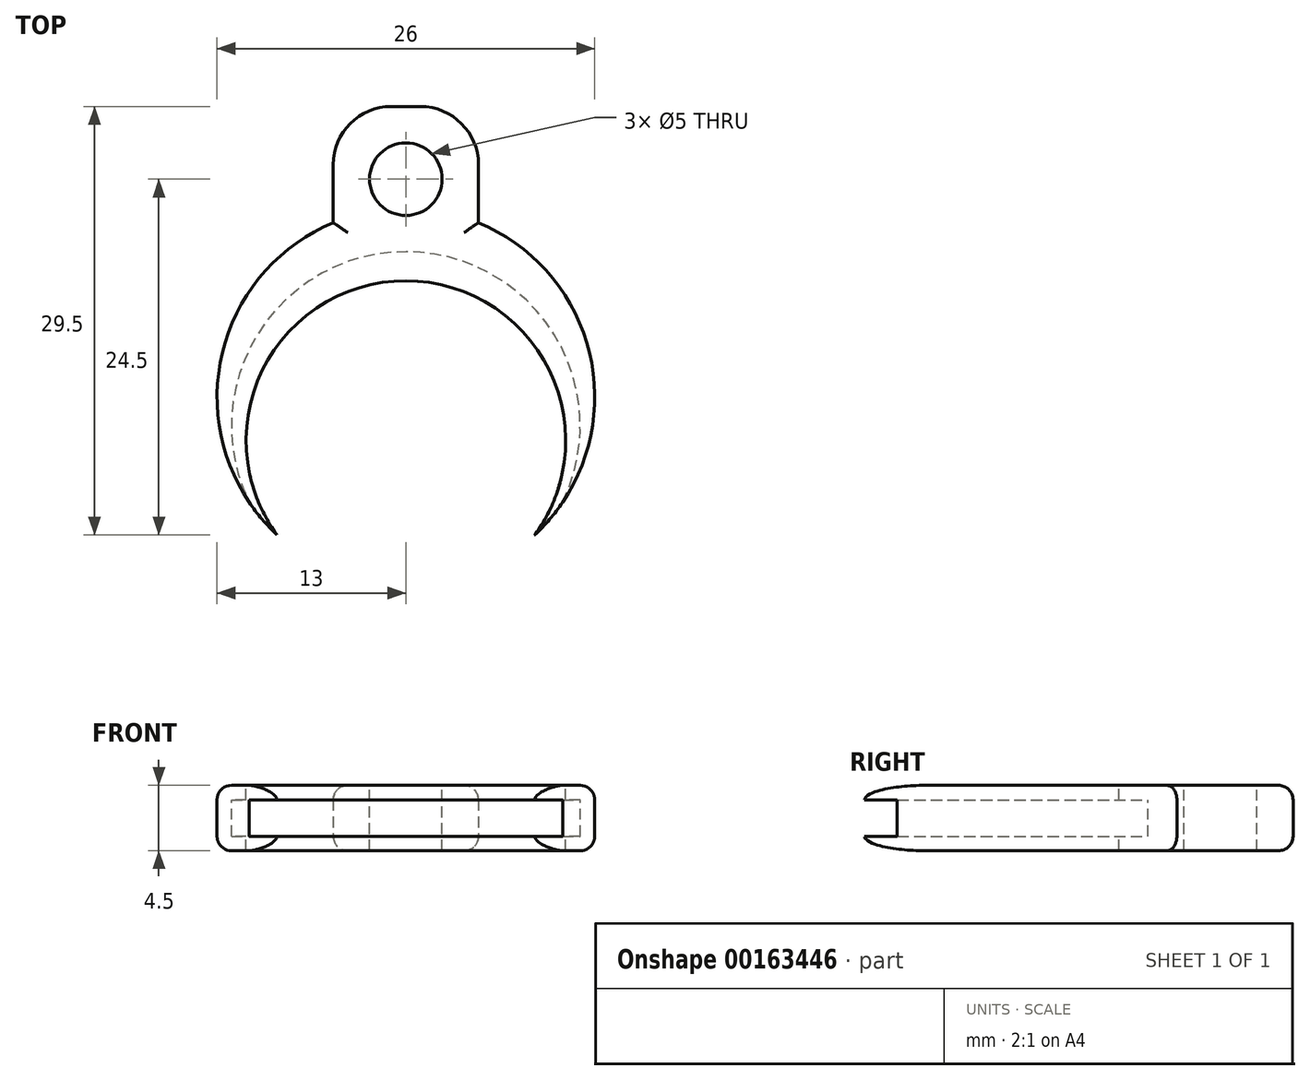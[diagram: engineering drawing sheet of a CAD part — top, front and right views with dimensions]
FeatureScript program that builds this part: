
annotation { "Feature Type Name" : "Feature", "Feature Type Description" : "" }
export const myFeature = defineFeature(function(context is Context, id is Id, definition is map)
    precondition{}
    {
        {
            var Q0;
            Q0=qCreatedBy(makeId("Top.planeOp"),FACE);
            var sketch = newSketch(context, id + "F0", { "sketchPlane" : qUnion([Q0])});
            skCircle(sketch, "E0", {"center": v(0, 0) * mm, "radius": 13 * mm});
            skLineSegment(sketch, "E1.bottom", {"start": v(-5, 12) * mm, "end": v(5, 12) * mm});
            skLineSegment(sketch, "E1.top", {"start": v(-5, 20) * mm, "end": v(5, 20) * mm});
            skLineSegment(sketch, "E1.left", {"start": v(-5, 12) * mm, "end": v(-5, 20) * mm});
            skLineSegment(sketch, "E1.right", {"start": v(5, 12) * mm, "end": v(5, 20) * mm});
            skSolve(sketch);
        }
        {
            var Q0;
            Q0 = qSketchRegion(id + "F0", true);
            extrude(context, id + "F1", {"entities" : qUnion([Q0]), "depth" : 4.5 * mm});
        }
        {
            var Q0;
            Q0=makeQuery(id+"F1.opExtrude","SWEPT_EDGE",EDGE,{"disambiguationData":[OSD([sQuery(id+"F0.wireOp",EDGE,"E1.top"),sQuery(id+"F0.wireOp",EDGE,"E1.right")])]});
            var Q1;
            Q1=makeQuery(id+"F1.opExtrude","SWEPT_EDGE",EDGE,{"disambiguationData":[OSD([sQuery(id+"F0.wireOp",EDGE,"E1.top"),sQuery(id+"F0.wireOp",EDGE,"E1.left")])]});
            fillet(context, id + "F2", {"entities" : qUnion([Q0, Q1]), "radius" : 4 * mm, "tangentPropagation" : true, "allowEdgeOverflow" : false});
        }
        {
            var Q0;
            Q0=makeQuery(id+"F1.opExtrude","CAP_FACE",FACE,{"disambiguationData":[OSD([sQuery(id+"F0.wireOp",EDGE,"E0"),sQuery(id+"F0.wireOp",EDGE,"E1.top"),sQuery(id+"F0.wireOp",EDGE,"E1.left"),sQuery(id+"F0.wireOp",EDGE,"E1.right")])],"isStart":false});
            var sketch = newSketch(context, id + "F3", { "sketchPlane" : qUnion([Q0])});
            skCircle(sketch, "E2", {"center": v(0, 15) * mm, "radius": 2.5 * mm});
            skSolve(sketch);
        }
        {
            var Q0;
            Q0 = qSketchRegion(id + "F3", true);
            extrude(context, id + "F4", {"entities" : qUnion([Q0]), "operationType" : NewBodyOperationType.REMOVE, "endBound" : BoundingType.THROUGH_ALL, "oppositeDirection" : true, "depth" : 25 * mm});
        }
        {
            var Q0;
            Q0=makeQuery(id+"F1.opExtrude","CAP_FACE",FACE,{"disambiguationData":[OSD([sQuery(id+"F0.wireOp",EDGE,"E0"),sQuery(id+"F0.wireOp",EDGE,"E1.top"),sQuery(id+"F0.wireOp",EDGE,"E1.left"),sQuery(id+"F0.wireOp",EDGE,"E1.right")])],"isStart":false});
            var sketch = newSketch(context, id + "F5", { "sketchPlane" : qUnion([Q0])});
            skCircle(sketch, "E3", {"center": v(0, -3) * mm, "radius": 11 * mm});
            skSolve(sketch);
        }
        {
            var Q0;
            Q0 = qSketchRegion(id + "F5", true);
            extrude(context, id + "F6", {"entities" : qUnion([Q0]), "operationType" : NewBodyOperationType.REMOVE, "oppositeDirection" : true, "depth" : 1 * mm});
        }
        {
            var Q0;
            Q0=makeQuery(id+"F6.boolean.opBoolean","COPY",FACE,{"derivedFrom":makeQuery(id+"F6.opExtrude","CAP_FACE",FACE,{"disambiguationData":[OSD([sQuery(id+"F5.wireOp",EDGE,"E3")])],"isStart":false})});
            var sketch = newSketch(context, id + "F7", { "sketchPlane" : qUnion([Q0])});
            skCircle(sketch, "E4", {"center": v(0, -2) * mm, "radius": 12 * mm});
            skSolve(sketch);
        }
        {
            var Q0;
            Q0 = qSketchRegion(id + "F7", true);
            extrude(context, id + "F8", {"entities" : qUnion([Q0]), "operationType" : NewBodyOperationType.REMOVE, "oppositeDirection" : true, "depth" : 2.5 * mm});
        }
        {
            var Q0;
            Q0=makeQuery(id+"F8.boolean.opBoolean","COPY",FACE,{"derivedFrom":makeQuery(id+"F8.opExtrude","CAP_FACE",FACE,{"disambiguationData":[OSD([sQuery(id+"F7.wireOp",EDGE,"E4")])],"isStart":false})});
            var sketch = newSketch(context, id + "F9", { "sketchPlane" : qUnion([Q0])});
            skCircle(sketch, "E5", {"center": v(0, -3) * mm, "radius": 11 * mm});
            skSolve(sketch);
        }
        {
            var Q0;
            Q0 = qSketchRegion(id + "F9", true);
            extrude(context, id + "F10", {"entities" : qUnion([Q0]), "operationType" : NewBodyOperationType.REMOVE, "endBound" : BoundingType.THROUGH_ALL, "oppositeDirection" : true, "depth" : 25 * mm});
        }
        {
            var Q0;
            {var subQ0=sQuery(id+"F0.wireOp",EDGE,"E0");var subQ1=sQuery(id+"F0.wireOp",EDGE,"E1.right");Q0=makeQuery(id+"F6.boolean.opBoolean","SPLIT",EDGE,{"disambiguationData":[TD([makeQuery(id+"F1.opExtrude","SWEPT_FACE",FACE,{"disambiguationData":[OSD([subQ1])]})])],"derivedFrom":makeQuery(id+"F1.opExtrude","CAP_EDGE",EDGE,{"disambiguationData":[OSD([subQ0])],"isStart":false})});}
            var Q1;
            Q1=makeQuery(id+"F1.opExtrude","CAP_EDGE",EDGE,{"disambiguationData":[OSD([sQuery(id+"F0.wireOp",EDGE,"E1.right")])],"isStart":false});
            var Q2;
            {var subQ0=sQuery(id+"F0.wireOp",EDGE,"E0");var subQ1=sQuery(id+"F0.wireOp",EDGE,"E1.left");Q2=makeQuery(id+"F6.boolean.opBoolean","SPLIT",EDGE,{"disambiguationData":[TD([makeQuery(id+"F1.opExtrude","SWEPT_FACE",FACE,{"disambiguationData":[OSD([subQ1])]})])],"derivedFrom":makeQuery(id+"F1.opExtrude","CAP_EDGE",EDGE,{"disambiguationData":[OSD([subQ0])],"isStart":false})});}
            var Q3;
            {var subQ0=sQuery(id+"F0.wireOp",EDGE,"E0");var subQ1=sQuery(id+"F0.wireOp",EDGE,"E1.right");Q3=makeQuery(id+"F10.boolean.opBoolean","SPLIT",EDGE,{"disambiguationData":[TD([makeQuery(id+"F1.opExtrude","SWEPT_FACE",FACE,{"disambiguationData":[OSD([subQ1])]})])],"derivedFrom":makeQuery(id+"F1.opExtrude","CAP_EDGE",EDGE,{"disambiguationData":[OSD([subQ0])],"isStart":true})});}
            var Q4;
            {var subQ0=sQuery(id+"F0.wireOp",EDGE,"E0");var subQ1=sQuery(id+"F0.wireOp",EDGE,"E1.left");Q4=makeQuery(id+"F10.boolean.opBoolean","SPLIT",EDGE,{"disambiguationData":[TD([makeQuery(id+"F1.opExtrude","SWEPT_FACE",FACE,{"disambiguationData":[OSD([subQ1])]})])],"derivedFrom":makeQuery(id+"F1.opExtrude","CAP_EDGE",EDGE,{"disambiguationData":[OSD([subQ0])],"isStart":true})});}
            var Q5;
            {var subQ0=sQuery(id+"F0.wireOp",EDGE,"E1.left");var subQ1=sQuery(id+"F0.wireOp",EDGE,"E1.top");Q5=makeQuery(id+"F2.opFillet","BLEND_EDGE",EDGE,{"blendedFrom":[makeQuery(id+"F1.opExtrude","SWEPT_EDGE",EDGE,{"disambiguationData":[OSD([subQ1,subQ0])]}),makeQuery(id+"F1.opExtrude","CAP_FACE",FACE,{"disambiguationData":[OSD([sQuery(id+"F0.wireOp",EDGE,"E0"),subQ1,subQ0,sQuery(id+"F0.wireOp",EDGE,"E1.right")])],"isStart":true})],"blendedInto":[makeQuery(id+"F1.opExtrude","CAP_FACE",FACE,{"disambiguationData":[OSD([sQuery(id+"F0.wireOp",EDGE,"E0"),subQ1,subQ0,sQuery(id+"F0.wireOp",EDGE,"E1.right")])],"isStart":true})]});}
            fillet(context, id + "F11", {"entities" : qUnion([Q0, Q1, Q2, Q3, Q4, Q5]), "radius" : 1 * mm, "tangentPropagation" : true, "allowEdgeOverflow" : false});
        }
    });
